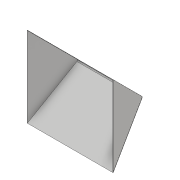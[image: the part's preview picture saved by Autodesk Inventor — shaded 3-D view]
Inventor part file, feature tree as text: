
AUTODESK INVENTOR PART (.ipt)
format: ipt  version: 2017 (Build 210142000, 142)  size: 155,136 bytes
history: native  units: mm
features: extrude x5, sketch x5, projected_geometry x3
ambient origin geometry x8: Origin, YZ Plane, XZ Plane, XY Plane, X Axis, Y Axis, Z Axis, Center Point
bodies: Solid1 (feature_tree)
feature tree (13):
  extrude  "Extrusion1"  Depth=200.0mm
  extrude  "Extrusion2"  Depth=0.8mm
  extrude  "Extrusion3"  Depth=200.0mm TaperAngle=0.0deg
  extrude  "Extrusion4"  TaperAngle=105.0deg  [1 undecoded]
  extrude  "Extrusion5"  Depth=0.8mm TaperAngle=0.0deg
  sketch  "Sketch1"  dims[d0=45.0deg d1=200.0mm]
  sketch  "Sketch4"  dims[d2=0.8mm d3=0.8mm]
  projected_geometry  "Projected Loop1"
  sketch  "Sketch5"  dims[d4=200.0mm d5=300.0mm d6=0.0mm]
  projected_geometry  "Projected Loop2"
  sketch  "Sketch7"  dims[d7=5.0mm d10=105.0deg]
  sketch  "Sketch8"  dims[d12=450.0mm d13=0.0mm d14=0.8mm d15=0.0mm d17=75.0deg d18=75.0deg d19=0.8mm d20=0.0mm d21=0.8mm d22=0.0mm]
  projected_geometry  "Projected Loop6"
note: 1 required parameter value undecoded (feature->parameter linkage not recoverable at this tier; creation-order binding heuristic only, values carry confidence <= 0.55)
